# Revit family: PRD_FrankeWS_MltFnctnDspnsrs_EXOSPaperTowelDispenserWasteBinCombination_EXOS602EX_602EB_602EW
name_source: partatom
category: Specialty Equipment
revit_build: Autodesk Revit 2018 (Build: 20190510_1515(x64)
units: mm (PartAtom-declared; Revit-internal decimal feet)

## family parameters
Cut with Voids When Loaded = No
Host = Face
OmniClass Number = 23.40.20.21.17
OmniClass Title = Paper Towel Dispensers, Disposal Units
Part Type = Normal
Room Calculation Point = No
Round Connector Dimension = Use Diameter
Shared = No

## types (3) — shared parameters
AssetType = Fixed
Category = Pr_40_70_22_52, Multi-function dispensers
CombinationPart1 = Paper towel dispenser
CombinationPart2 = Waste bin
Default Elevation = 800 mm  [stored 2.62467 ft]
DispenserMaterial = PRD_AR_StainlessSteel_SatinFinished
DurationUnit = year
Features = stainless steel, surface satin finished
FillingQuantity1 = 400
FillingQuantity1Uom = Pieces
FillingQuantity2 = 30
FillingQuantity2Uom = Liter
Finish = satin finished
IfcExportAs = IfcFurnitureType
IfcExportType = USERDEFINED
IntegralAccessories = incl. mounting bracket and mounting materials
IsBuiltIn = TRUE
Lock1 = Key-lock
Lock2 = Key-lock
MainColor = stainless steel
Manufacturer = KWC Group AG
ManufacturerName = KWC Group AG
Material = stainless steel
MaterialCode = 1.4301
MaterialThickness = 1.20 mm
NBSDescription = Multi-function dispensers
NBSReference = 45-35-72/384
NominalDepth = 251 mm  [stored 0.823491 ft]
NominalHeight = 1166 mm
NominalWidth = 304 mm  [stored 0.997375 ft]
ProductInformation = https://pim.kwc.com
Size = 304 x 1166 x 251 mm
SurfaceTreatment = InoxPlus (anti fingerprint)
TypeOfConsumable1 = Paper towel
TypeOfFixing = Screw
TypeOfMounting = Recessed mounting
URL = www.kwc.com
Uniclass2015Code = Pr_40_70_22_52
Uniclass2015Title = Multi-function dispensers
Uniclass2015Version = Products v1.17
Version = 1
WarrantyDurationUnit = year

## per-type parameters (varying)
| type | BIMObjectName | Description | GrossWeight | ManufacturerURL | ModelNumber | Name | NetWeight | PanelMaterial |
| EXOS602EX | PRD_AR_MultiFunctionDispensers_EXOSPaperTowelDispenserWasteBinCombination_EXOS602EX | Paper towel dispenser and waste bin combination for recessed mounting, stainless steel with satin finished, front with InoxPlus surface refinement for the reduction of finger marks and better cleaning characteristics (easy to clean), material thickness 1.2 mm, capacity paper towel dispenser 300 - 400 pieces of Z-folded paper depending on convolution, waste bin with approx. 30 liter capacity, integrated bag holder, includes mounting bracket and mounting materials. | 16.62 kg | www.kwc.com | 2030034626 | Paper Towel Dispenser Waste Bin Combination EXOS602EX | 15.62 kg | PRD_AR_StainlessSteel_SatinFinished |
| EXOS602EB | PRD_AR_MultiFunctionDispensers_EXOSPaperTowelDispenserWasteBinCombination_EXOS602EB | Paper towel dispenser and waste bin combination for recessed mounting, stainless steel with satin finished, black safety glass front panel, casing with InoxPlus surface refinement for the reduction of finger marks and better cleaning characteristics (easy to clean), material thickness 1.2 mm, capacity paper towel dispenser 300 - 400 pieces of Z-folded paper depending on convolution, waste bin with approx. 30 liter capacity, integrated bag holder, includes mounting bracket and mounting materials. | 18.46 kg | www.kwc.com
www.kwc.com | 2030034627 | Paper Towel Dispenser Waste Bin Combination EXOS602EB | 17.46 kg | PRD_AR_Glass_Black |
| EXOS602EW | PRD_AR_MultiFunctionDispensers_EXOSPaperTowelDispenserWasteBinCombination_EXOS602EW | Paper towel dispenser and waste bin combination for recessed mounting, stainless steel with satin finished, white safety glass front panel, casing with InoxPlus surface refinement for the reduction of finger marks and better cleaning characteristics (easy to clean), material thickness 1.2 mm, capacity paper towel dispenser 300 - 400 pieces of Z-folded paper depending on convolution, waste bin with approx. 30 liter capacity, integrated bag holder, includes mounting materials. | 18.46 kg | www.kwc.com | 2030034663 | Paper Towel Dispenser Waste Bin Combination EXOS602EW | 17.46 kg | PRD_AR_Glass_White |

note: column(s) folded — value = type name in every type: Model, ModelReference

note: [stored X ft] marks values corroborated as IEEE doubles in the binary element streams (Revit-internal decimal feet)

## geometry (parser evidence)
native form markers: Sweep x3
no freeform markers — native parametric forms only
